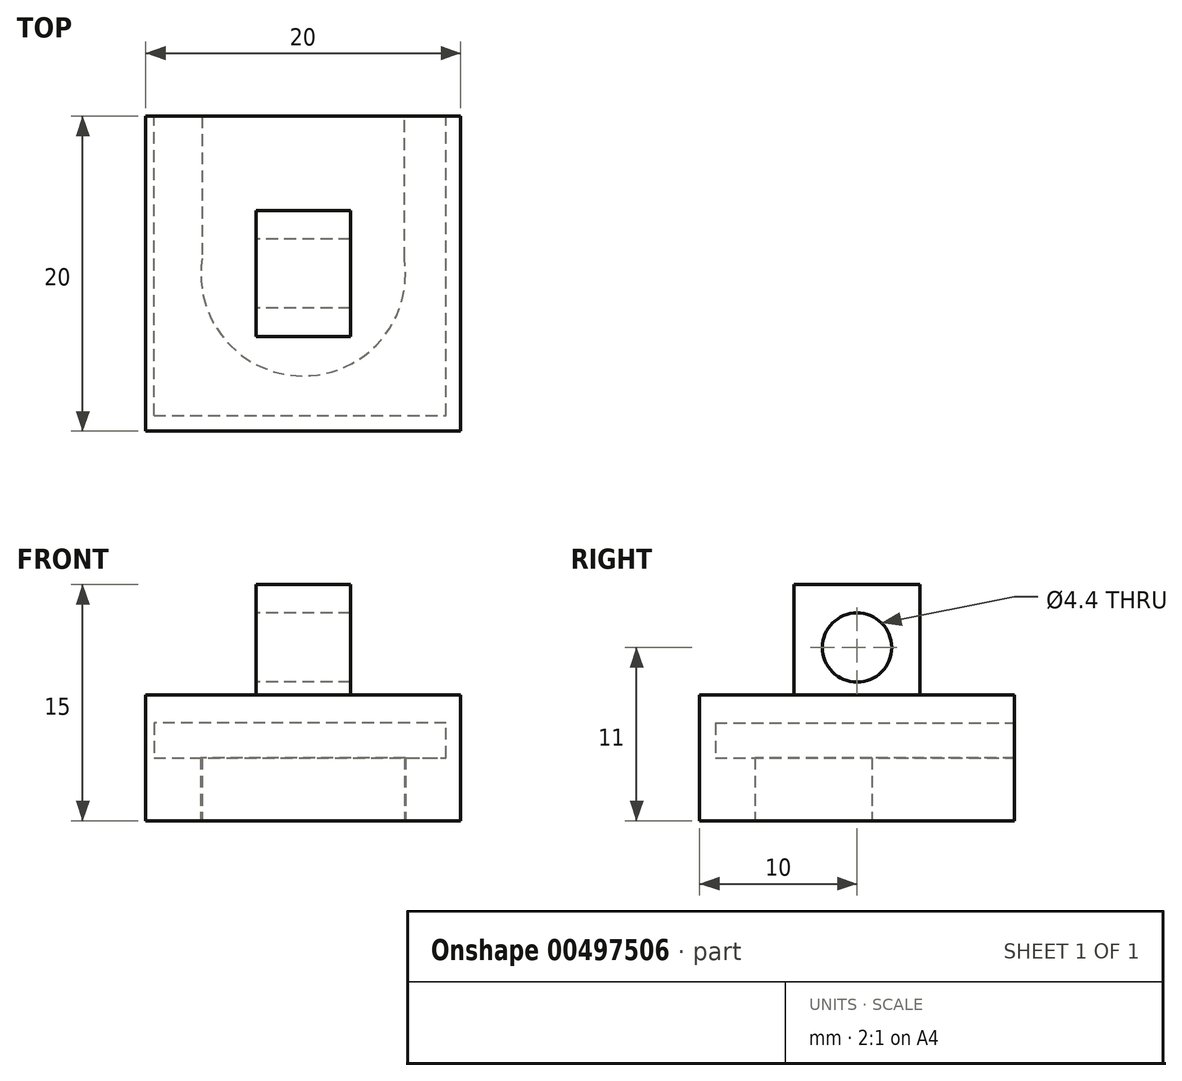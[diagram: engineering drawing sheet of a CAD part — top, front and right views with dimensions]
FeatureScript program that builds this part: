
annotation { "Feature Type Name" : "Feature", "Feature Type Description" : "" }
export const myFeature = defineFeature(function(context is Context, id is Id, definition is map)
    precondition{}
    {
        {
            var Q0;
            Q0=qCreatedBy(makeId("Top.planeOp"),FACE);
            var sketch = newSketch(context, id + "F0", { "sketchPlane" : qUnion([Q0])});
            skLineSegment(sketch, "E0.bottom", {"start": v(10, -10) * mm, "end": v(-10, -10) * mm});
            skLineSegment(sketch, "E0.top", {"start": v(10, 10) * mm, "end": v(-10, 10) * mm});
            skLineSegment(sketch, "E0.left", {"start": v(10, -10) * mm, "end": v(10, 10) * mm});
            skLineSegment(sketch, "E0.right", {"start": v(-10, -10) * mm, "end": v(-10, 10) * mm});
            skPoint(sketch, "E0.middle", {"position": v(0, 0) * mm});
            skSolve(sketch);
        }
        {
            var Q0;
            Q0=makeQuery(id+"F0.imprint","IMPRINT",FACE,{"disambiguationData":[TD([[makeQuery(id+"F0.imprint","IMPRINT",EDGE,{"derivedFrom":sQuery(id+"F0.wireOp",EDGE,"E0.bottom")}),-1.0]])]});
            extrude(context, id + "F1", {"entities" : qUnion([Q0]), "depth" : 8 * mm, "offsetDistance" : 25 * mm});
        }
        {
            var Q0;
            Q0=makeQuery(id+"F1.opExtrude","CAP_FACE",FACE,{"disambiguationData":[OSD([sQuery(id+"F0.wireOp",EDGE,"E0.bottom"),sQuery(id+"F0.wireOp",EDGE,"E0.top"),sQuery(id+"F0.wireOp",EDGE,"E0.left"),sQuery(id+"F0.wireOp",EDGE,"E0.right")])],"isStart":true});
            var sketch = newSketch(context, id + "F2", { "sketchPlane" : qUnion([Q0])});
            skCircle(sketch, "E1", {"center": v(0, 0) * mm, "radius": 6.5 * mm});
            skLineSegment(sketch, "E2", {"start": v(-6.43, -0.95) * mm, "end": v(6.43, -0.95) * mm});
            skLineSegment(sketch, "E3", {"start": v(6.43, -0.95) * mm, "end": v(6.43, -10) * mm});
            skLineSegment(sketch, "E4", {"start": v(6.43, -10) * mm, "end": v(-6.43, -10) * mm});
            skLineSegment(sketch, "E5", {"start": v(-6.43, -10) * mm, "end": v(-6.43, -0.95) * mm});
            skSolve(sketch);
        }
        {
            var Q0;
            {var subQ0=sQuery(id+"F2.wireOp",EDGE,"E2");Q0=makeQuery(id+"F2.imprint","IMPRINT",FACE,{"disambiguationData":[TD([[makeQuery(id+"F2.imprint","IMPRINT",EDGE,{"derivedFrom":subQ0}),1.0]])]});}
            var Q1;
            {var subQ0=sQuery(id+"F2.wireOp",EDGE,"E2");Q1=makeQuery(id+"F2.imprint","IMPRINT",FACE,{"disambiguationData":[TD([[makeQuery(id+"F2.imprint","IMPRINT",EDGE,{"derivedFrom":subQ0}),-1.0]])]});}
            var Q2;
            {var subQ3=sQuery(id+"F2.wireOp",EDGE,"E3");Q2=makeQuery(id+"F2.imprint","IMPRINT",FACE,{"disambiguationData":[TD([[makeQuery(id+"F2.imprint","IMPRINT",EDGE,{"derivedFrom":subQ3}),-1.0]])]});}
            extrude(context, id + "F3", {"entities" : qUnion([Q0, Q1, Q2]), "operationType" : NewBodyOperationType.REMOVE, "oppositeDirection" : true, "depth" : 4 * mm, "offsetDistance" : 25 * mm});
        }
        {
            var Q0;
            Q0=makeQuery(id+"F1.opExtrude","SWEPT_FACE",FACE,{"disambiguationData":[OSD([sQuery(id+"F0.wireOp",EDGE,"E0.top")])]});
            var sketch = newSketch(context, id + "F4", { "sketchPlane" : qUnion([Q0])});
            skLineSegment(sketch, "E6", {"start": v(9.47, 4) * mm, "end": v(-9.09, 4) * mm});
            skLineSegment(sketch, "E7", {"start": v(-9.09, 4) * mm, "end": v(-9.09, 6.21) * mm});
            skLineSegment(sketch, "E8", {"start": v(-9.09, 6.21) * mm, "end": v(9.47, 6.21) * mm});
            skLineSegment(sketch, "E9", {"start": v(9.47, 6.21) * mm, "end": v(9.47, 4) * mm});
            skSolve(sketch);
        }
        {
            var Q0;
            {var subQ0=sQuery(id+"F4.wireOp",EDGE,"E7");Q0=makeQuery(id+"F4.imprint","IMPRINT",FACE,{"disambiguationData":[TD([[makeQuery(id+"F4.imprint","IMPRINT",EDGE,{"derivedFrom":subQ0}),-1.0]])]});}
            extrude(context, id + "F5", {"entities" : qUnion([Q0]), "operationType" : NewBodyOperationType.REMOVE, "oppositeDirection" : true, "depth" : 19 * mm, "offsetDistance" : 25 * mm});
        }
        {
            var Q0;
            Q0=makeQuery(id+"F1.opExtrude","CAP_FACE",FACE,{"disambiguationData":[OSD([sQuery(id+"F0.wireOp",EDGE,"E0.bottom"),sQuery(id+"F0.wireOp",EDGE,"E0.top"),sQuery(id+"F0.wireOp",EDGE,"E0.left"),sQuery(id+"F0.wireOp",EDGE,"E0.right")])],"isStart":false});
            var sketch = newSketch(context, id + "F6", { "sketchPlane" : qUnion([Q0])});
            skLineSegment(sketch, "E10.bottom", {"start": v(3, -4) * mm, "end": v(-3, -4) * mm});
            skLineSegment(sketch, "E10.top", {"start": v(3, 4) * mm, "end": v(-3, 4) * mm});
            skLineSegment(sketch, "E10.left", {"start": v(3, -4) * mm, "end": v(3, 4) * mm});
            skLineSegment(sketch, "E10.right", {"start": v(-3, -4) * mm, "end": v(-3, 4) * mm});
            skPoint(sketch, "E10.middle", {"position": v(0, 0) * mm});
            skSolve(sketch);
        }
        {
            var Q0;
            Q0=makeQuery(id+"F6.imprint","IMPRINT",FACE,{"disambiguationData":[TD([[makeQuery(id+"F6.imprint","IMPRINT",EDGE,{"derivedFrom":sQuery(id+"F6.wireOp",EDGE,"E10.bottom")}),-1.0]])]});
            extrude(context, id + "F7", {"entities" : qUnion([Q0]), "operationType" : NewBodyOperationType.ADD, "depth" : 7 * mm, "offsetDistance" : 25 * mm});
        }
        {
            var Q0;
            Q0=makeQuery(id+"F7.opExtrude","SWEPT_FACE",FACE,{"disambiguationData":[OSD([sQuery(id+"F6.wireOp",EDGE,"E10.right")])]});
            var sketch = newSketch(context, id + "F8", { "sketchPlane" : qUnion([Q0])});
            skCircle(sketch, "E11", {"center": v(0, 11) * mm, "radius": 2.2 * mm});
            skSolve(sketch);
        }
        {
            var Q0;
            Q0=makeQuery(id+"F8.imprint","IMPRINT",FACE,{"disambiguationData":[TD([[makeQuery(id+"F8.imprint","IMPRINT",EDGE,{"derivedFrom":sQuery(id+"F8.wireOp",EDGE,"E11")}),1.0]])]});
            extrude(context, id + "F9", {"entities" : qUnion([Q0]), "operationType" : NewBodyOperationType.REMOVE, "oppositeDirection" : true, "depth" : 6 * mm, "offsetDistance" : 25 * mm});
        }
    });
